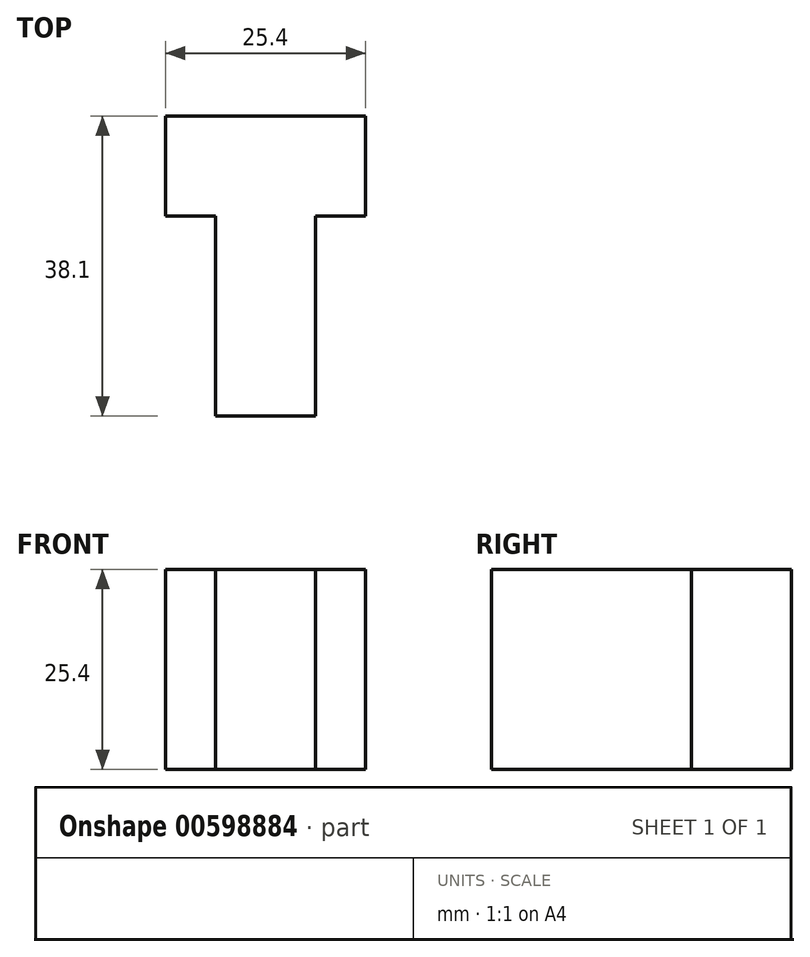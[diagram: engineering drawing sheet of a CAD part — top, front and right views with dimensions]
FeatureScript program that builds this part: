
annotation { "Feature Type Name" : "Feature", "Feature Type Description" : "" }
export const myFeature = defineFeature(function(context is Context, id is Id, definition is map)
    precondition{}
    {
        {
            var Q0;
            Q0=qCreatedBy(makeId("Top.planeOp"),FACE);
            var sketch = newSketch(context, id + "F0", { "sketchPlane" : qUnion([Q0])});
            skLineSegment(sketch, "E0", {"start": v(0, 0) * mm, "end": v(0, 25.4) * mm});
            skLineSegment(sketch, "E1", {"start": v(0, 25.4) * mm, "end": v(-6.35, 25.4) * mm});
            skLineSegment(sketch, "E2", {"start": v(-6.35, 25.4) * mm, "end": v(-6.35, 38.1) * mm});
            skLineSegment(sketch, "E3", {"start": v(-6.35, 38.1) * mm, "end": v(19.05, 38.1) * mm});
            skLineSegment(sketch, "E4", {"start": v(19.05, 38.1) * mm, "end": v(19.05, 25.4) * mm});
            skLineSegment(sketch, "E5", {"start": v(19.05, 25.4) * mm, "end": v(12.7, 25.4) * mm});
            skLineSegment(sketch, "E6", {"start": v(12.7, 25.4) * mm, "end": v(12.7, 0) * mm});
            skLineSegment(sketch, "E7", {"start": v(12.7, 0) * mm, "end": v(0, 0) * mm});
            skSolve(sketch);
        }
        {
            var Q0;
            Q0 = qSketchRegion(id + "F0", true);
            extrude(context, id + "F1", {"entities" : qUnion([Q0]), "depth" : 25.4 * mm, "offsetDistance" : 25.4 * mm});
        }
    });
